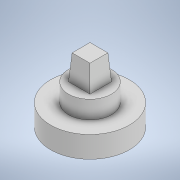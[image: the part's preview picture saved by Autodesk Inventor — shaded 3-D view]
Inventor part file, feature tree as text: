
AUTODESK INVENTOR PART (.ipt)
format: ipt  version: 2021 (Build 250183000, 183)  size: 123,392 bytes
history: native  units: mm
features: sketch x4, extrude x2, plane x1, loft x1
ambient origin geometry x8: Origin, YZ Plane, XZ Plane, XY Plane, X Axis, Y Axis, Z Axis, Center Point
bodies: Solid1 (feature_tree)
feature tree (8):
  extrude  "Extrusion1"  Depth=6.0mm TaperAngle=0.0deg
  extrude  "Extrusion2"  Depth=5.0mm TaperAngle=0.0deg
  sketch  "Sketch3"  dims[d6=6.0mm d7=6.0mm]
  plane  "Work Plane1"
  loft  "Loft1"
  sketch  "Sketch1"  dims[d0=22.0mm d1=6.0mm d2=0.0mm]
  sketch  "Sketch2"  dims[d3=12.0mm d4=5.0mm d5=0.0mm]
  sketch  "Sketch4"  dims[d8=7.0mm d9=5.0mm d10=5.0mm d11=0.0mm d12=90.0deg d13=0.0mm d14=90.0deg]
